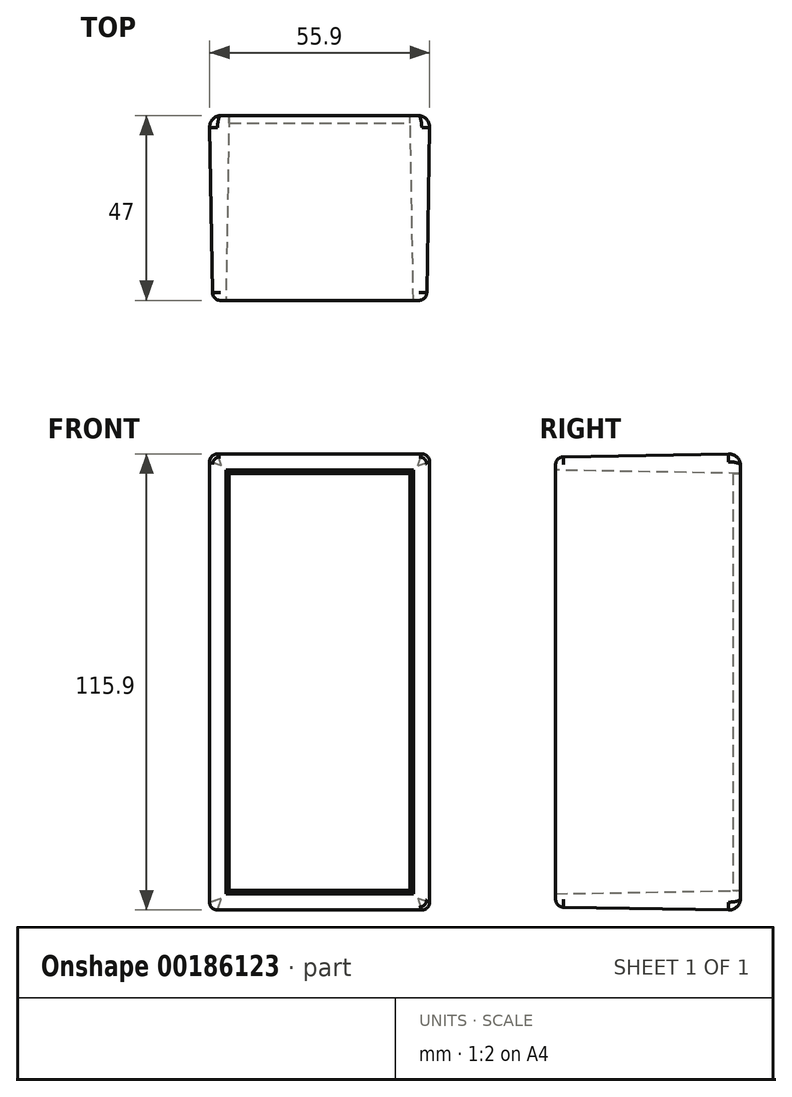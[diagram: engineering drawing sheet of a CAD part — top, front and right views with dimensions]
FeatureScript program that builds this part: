
annotation { "Feature Type Name" : "Feature", "Feature Type Description" : "" }
export const myFeature = defineFeature(function(context is Context, id is Id, definition is map)
    precondition{}
    {
        {
            var Q0;
            Q0=qCreatedBy(makeId("Front.planeOp"),FACE);
            var sketch = newSketch(context, id + "F0", { "sketchPlane" : qUnion([Q0])});
            skLineSegment(sketch, "E0.bottom", {"start": v(-28, 58) * mm, "end": v(28, 58) * mm});
            skLineSegment(sketch, "E0.top", {"start": v(-28, -58) * mm, "end": v(28, -58) * mm});
            skLineSegment(sketch, "E0.left", {"start": v(-28, 58) * mm, "end": v(-28, -58) * mm});
            skLineSegment(sketch, "E0.right", {"start": v(28, 58) * mm, "end": v(28, -58) * mm});
            skPoint(sketch, "E1", {"position": v(0, 58) * mm});
            skPoint(sketch, "E2", {"position": v(0, -58) * mm});
            skPoint(sketch, "E3", {"position": v(28, 0) * mm});
            skPoint(sketch, "E4", {"position": v(-28, 0) * mm});
            skLineSegment(sketch, "E5.bottom", {"start": v(-23, 53) * mm, "end": v(23, 53) * mm});
            skLineSegment(sketch, "E5.top", {"start": v(-23, -53) * mm, "end": v(23, -53) * mm});
            skLineSegment(sketch, "E5.left", {"start": v(-23, 53) * mm, "end": v(-23, -53) * mm});
            skLineSegment(sketch, "E5.right", {"start": v(23, 53) * mm, "end": v(23, -53) * mm});
            skPoint(sketch, "E6", {"position": v(0, 53) * mm});
            skPoint(sketch, "E7", {"position": v(23, 0) * mm});
            skSolve(sketch);
        }
        {
            var Q0;
            Q0 = qSketchRegion(id + "F0", true);
            extrude(context, id + "F1", {"entities" : qUnion([Q0]), "depth" : 47 * mm, "hasDraft" : true, "draftAngle" : 1 * degree, "draftPullDirection" : true});
        }
        {
            var Q0;
            Q0=makeQuery(id+"F0.imprint","IMPRINT",FACE,{"disambiguationData":[TD([[makeQuery(id+"F0.imprint","IMPRINT",EDGE,{"derivedFrom":sQuery(id+"F0.wireOp",EDGE,"E5.bottom")}),-1.0]])]});
            extrude(context, id + "F2", {"entities" : qUnion([Q0]), "operationType" : NewBodyOperationType.ADD, "depth" : 2 * mm});
        }
        {
            var Q0;
            Q0=makeQuery(id+"F1.opExtrude","CAP_EDGE",EDGE,{"disambiguationData":[OSD([sQuery(id+"F0.wireOp",EDGE,"E0.right")])],"isStart":true});
            var Q1;
            Q1=makeQuery(id+"F1.opExtrude","CAP_EDGE",EDGE,{"disambiguationData":[OSD([sQuery(id+"F0.wireOp",EDGE,"E0.top")])],"isStart":true});
            var Q2;
            Q2=makeQuery(id+"F1.opExtrude","CAP_EDGE",EDGE,{"disambiguationData":[OSD([sQuery(id+"F0.wireOp",EDGE,"E0.left")])],"isStart":true});
            var Q3;
            Q3=makeQuery(id+"F1.opExtrude","CAP_EDGE",EDGE,{"disambiguationData":[OSD([sQuery(id+"F0.wireOp",EDGE,"E0.bottom")])],"isStart":true});
            fillet(context, id + "F3", {"entities" : qUnion([Q0, Q1, Q2, Q3]), "radius" : 3 * mm, "tangentPropagation" : true, "allowEdgeOverflow" : false});
        }
        {
            var Q0;
            Q0=makeQuery(id+"F1.opExtrude","SWEPT_EDGE",EDGE,{"disambiguationData":[OSD([sQuery(id+"F0.wireOp",EDGE,"E0.bottom"),sQuery(id+"F0.wireOp",EDGE,"E0.right")])]});
            var Q1;
            Q1=makeQuery(id+"F1.opExtrude","SWEPT_EDGE",EDGE,{"disambiguationData":[OSD([sQuery(id+"F0.wireOp",EDGE,"E0.bottom"),sQuery(id+"F0.wireOp",EDGE,"E0.left")])]});
            var Q2;
            Q2=makeQuery(id+"F1.opExtrude","SWEPT_EDGE",EDGE,{"disambiguationData":[OSD([sQuery(id+"F0.wireOp",EDGE,"E0.top"),sQuery(id+"F0.wireOp",EDGE,"E0.left")])]});
            var Q3;
            Q3=makeQuery(id+"F1.opExtrude","SWEPT_EDGE",EDGE,{"disambiguationData":[OSD([sQuery(id+"F0.wireOp",EDGE,"E0.top"),sQuery(id+"F0.wireOp",EDGE,"E0.right")])]});
            var Q4;
            Q4=makeQuery(id+"F1.opExtrude","CAP_EDGE",EDGE,{"disambiguationData":[OSD([sQuery(id+"F0.wireOp",EDGE,"E0.top")])],"isStart":false});
            var Q5;
            Q5=makeQuery(id+"F1.opExtrude","CAP_EDGE",EDGE,{"disambiguationData":[OSD([sQuery(id+"F0.wireOp",EDGE,"E0.left")])],"isStart":false});
            var Q6;
            Q6=makeQuery(id+"F1.opExtrude","CAP_EDGE",EDGE,{"disambiguationData":[OSD([sQuery(id+"F0.wireOp",EDGE,"E0.bottom")])],"isStart":false});
            var Q7;
            Q7=makeQuery(id+"F1.opExtrude","CAP_EDGE",EDGE,{"disambiguationData":[OSD([sQuery(id+"F0.wireOp",EDGE,"E0.right")])],"isStart":false});
            fillet(context, id + "F4", {"entities" : qUnion([Q0, Q1, Q2, Q3, Q4, Q5, Q6, Q7]), "radius" : 2 * mm, "tangentPropagation" : true, "allowEdgeOverflow" : false});
        }
    });
